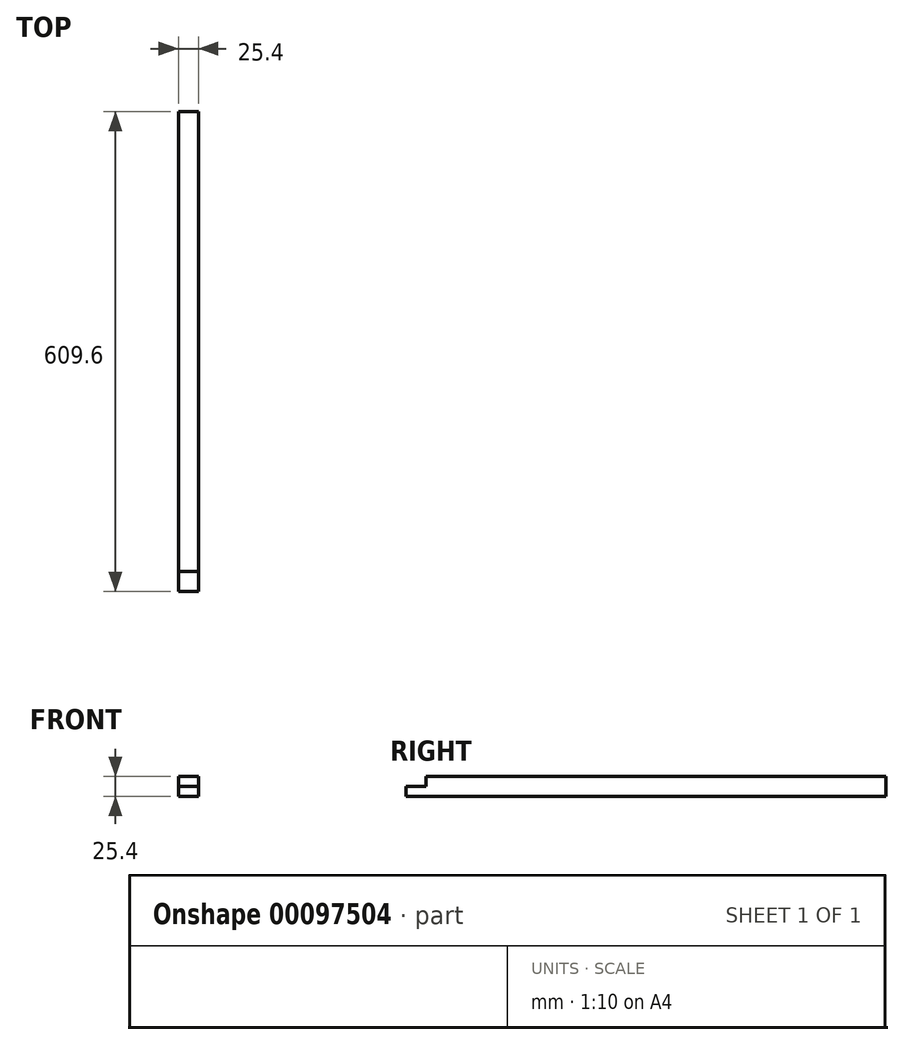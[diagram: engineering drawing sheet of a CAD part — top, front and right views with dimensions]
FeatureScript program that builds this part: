
annotation { "Feature Type Name" : "Feature", "Feature Type Description" : "" }
export const myFeature = defineFeature(function(context is Context, id is Id, definition is map)
    precondition{}
    {
        {
            var Q0;
            Q0=qCreatedBy(makeId("Front.planeOp"),FACE);
            var sketch = newSketch(context, id + "F0", { "sketchPlane" : qUnion([Q0])});
            skLineSegment(sketch, "E0.bottom", {"start": v(0, 0) * mm, "end": v(25.4, 0) * mm});
            skLineSegment(sketch, "E0.top", {"start": v(0, 25.4) * mm, "end": v(25.4, 25.4) * mm});
            skLineSegment(sketch, "E0.left", {"start": v(0, 0) * mm, "end": v(0, 25.4) * mm});
            skLineSegment(sketch, "E0.right", {"start": v(25.4, 0) * mm, "end": v(25.4, 25.4) * mm});
            skSolve(sketch);
        }
        {
            var Q0;
            Q0=makeQuery(id+"F0.imprint","IMPRINT",FACE,{"disambiguationData":[TD([[makeQuery(id+"F0.imprint","IMPRINT",EDGE,{"derivedFrom":sQuery(id+"F0.wireOp",EDGE,"E0.bottom")}),1.0]])]});
            extrude(context, id + "F1", {"entities" : qUnion([Q0]), "oppositeDirection" : true, "depth" : 609.6 * mm});
        }
        {
            var Q0;
            Q0=makeQuery(id+"F1.opExtrude","SWEPT_FACE",FACE,{"disambiguationData":[OSD([sQuery(id+"F0.wireOp",EDGE,"E0.top")])]});
            var sketch = newSketch(context, id + "F2", { "sketchPlane" : qUnion([Q0])});
            skLineSegment(sketch, "E1.bottom", {"start": v(0, 0) * mm, "end": v(25.4, 0) * mm});
            skLineSegment(sketch, "E1.top", {"start": v(0, 25.4) * mm, "end": v(25.4, 25.4) * mm});
            skLineSegment(sketch, "E1.left", {"start": v(0, 0) * mm, "end": v(0, 25.4) * mm});
            skLineSegment(sketch, "E1.right", {"start": v(25.4, 0) * mm, "end": v(25.4, 25.4) * mm});
            skSolve(sketch);
        }
        {
            var Q0;
            Q0=makeQuery(id+"F2.imprint","IMPRINT",FACE,{"disambiguationData":[TD([[makeQuery(id+"F2.imprint","IMPRINT",EDGE,{"derivedFrom":sQuery(id+"F2.wireOp",EDGE,"E1.bottom")}),1.0]])]});
            extrude(context, id + "F3", {"entities" : qUnion([Q0]), "operationType" : NewBodyOperationType.REMOVE, "oppositeDirection" : true, "depth" : 12.7 * mm});
        }
    });
